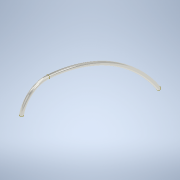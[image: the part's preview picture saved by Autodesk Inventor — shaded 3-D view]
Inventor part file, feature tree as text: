
AUTODESK INVENTOR PART (.ipt)
format: ipt  version: 2022 (Build 260153000, 153)  size: 137,728 bytes
history: native  units: in
note: dims shown in document units (in); Inventor stores cm internally (conversion verified against a paired STEP export)
features: sketch x2, sweep x1
ambient origin geometry x8: Origin, YZ Plane, XZ Plane, XY Plane, X Axis, Y Axis, Z Axis, Center Point
bodies: Solid1 (feature_tree)
feature tree (3):
  sweep  "Sweep1"
  sketch  "Sketch3"  dims[d10=0.001in d11=0.0059in]
  sketch  "Sketch4"  dims[d12=0.013in d13=0.0335in d14=90.0deg d15=0.0in d16=0.0in]
